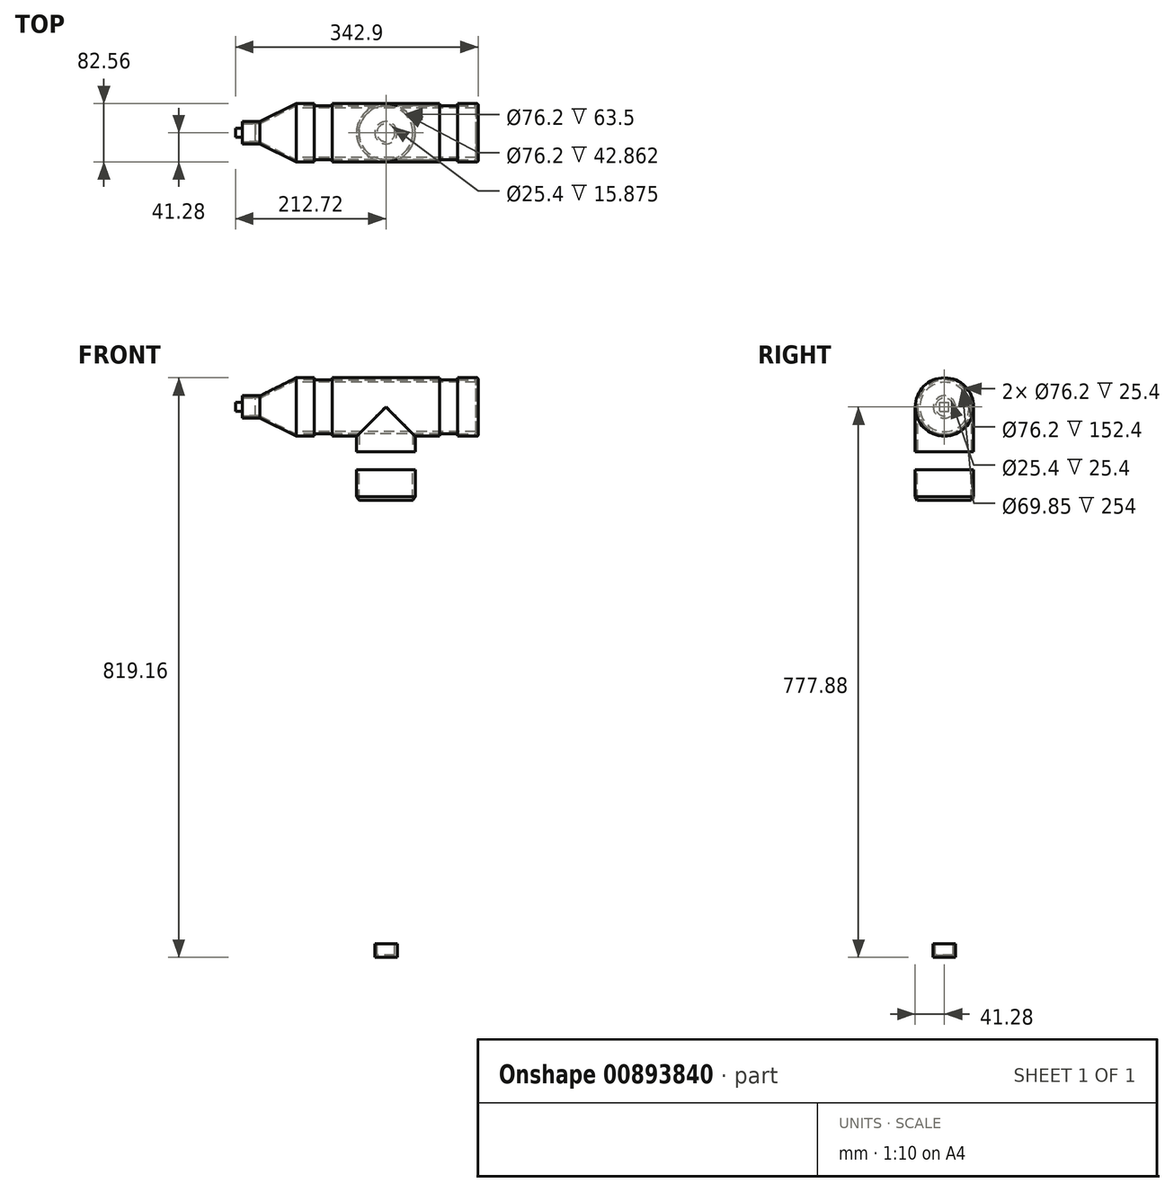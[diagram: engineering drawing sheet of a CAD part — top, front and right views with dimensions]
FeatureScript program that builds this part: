
annotation { "Feature Type Name" : "Feature", "Feature Type Description" : "" }
export const myFeature = defineFeature(function(context is Context, id is Id, definition is map)
    precondition{}
    {
        {
            var Q0;
            Q0=qCreatedBy(makeId("Top.planeOp"),FACE);
            var sketch = newSketch(context, id + "F0", { "sketchPlane" : qUnion([Q0])});
            skCircle(sketch, "E0", {"center": v(0, 0) * mm, "radius": 9.53 * mm});
            skCircle(sketch, "E1", {"center": v(0, 0) * mm, "radius": 12.7 * mm});
            skSolve(sketch);
        }
        {
            var Q0;
            Q0=makeQuery(id+"F0.imprint","IMPRINT",FACE,{"disambiguationData":[TD([[makeQuery(id+"F0.imprint","IMPRINT",EDGE,{"derivedFrom":sQuery(id+"F0.wireOp",EDGE,"E0")}),-1.0]])]});
            extrude(context, id + "F1", {"entities" : qUnion([Q0]), "depth" : 609.6 * mm, "offsetDistance" : 25.4 * mm});
        }
        {
            var Q0;
            Q0=qCreatedBy(makeId("Front.planeOp"),FACE);
            var sketch = newSketch(context, id + "F2", { "sketchPlane" : qUnion([Q0])});
            skLineSegment(sketch, "E2", {"start": v(12.7, 584.2) * mm, "end": v(12.7, 609.6) * mm});
            skLineSegment(sketch, "E3", {"start": v(12.7, 584.2) * mm, "end": v(15.87, 584.2) * mm});
            skLineSegment(sketch, "E4", {"start": v(15.87, 584.2) * mm, "end": v(15.87, 609.6) * mm});
            skLineSegment(sketch, "E5", {"start": v(38.1, 647.7) * mm, "end": v(38.1, 685.8) * mm});
            skLineSegment(sketch, "E6", {"start": v(38.1, 685.8) * mm, "end": v(41.27, 685.8) * mm});
            skLineSegment(sketch, "E7", {"start": v(41.27, 685.8) * mm, "end": v(41.27, 647.7) * mm});
            skLineSegment(sketch, "E8", {"start": v(38.1, 647.7) * mm, "end": v(12.7, 609.6) * mm});
            skLineSegment(sketch, "E9", {"start": v(41.27, 647.7) * mm, "end": v(15.87, 609.6) * mm});
            skLineSegment(sketch, "E10", {"start": v(0, 685.8) * mm, "end": v(0, 584.2) * mm, "construction": true});
            skSolve(sketch);
        }
        {
            var Q0;
            Q0=makeQuery(id+"F2.imprint","IMPRINT",FACE,{"disambiguationData":[TD([[makeQuery(id+"F2.imprint","IMPRINT",EDGE,{"derivedFrom":sQuery(id+"F2.wireOp",EDGE,"E2")}),-1.0]])]});
            var Q1;
            Q1=sQuery(id+"F2.wireOp",EDGE,"E10");
            revolve(context, id + "F3", {"surfaceOperationType" : NewSurfaceOperationType.NEW, "entities" : qUnion([Q0]), "axis" : qUnion([Q1]), "revolveType" : RevolveType.FULL});
        }
        {
            var Q0;
            Q0=qCreatedBy(makeId("Top.planeOp"),FACE);
            var sketch = newSketch(context, id + "F4", { "sketchPlane" : qUnion([Q0])});
            skCircle(sketch, "E11", {"center": v(0, 0) * mm, "radius": 38.1 * mm});
            skCircle(sketch, "E12", {"center": v(0, 0) * mm, "radius": 34.93 * mm});
            skSolve(sketch);
        }
        {
            var Q0;
            Q0 = qSketchRegion(id + "F4", true);
            extrude(context, id + "F5", {"entities" : qUnion([Q0]), "depth" : 736.6 * mm, "offsetDistance" : 25.4 * mm, "hasSecondDirection" : true, "secondDirectionOppositeDirection" : false, "secondDirectionDepth" : 647.7 * mm});
        }
        {
            var Q0;
            Q0=makeQuery(id+"F3.opRevolve","SWEPT_FACE",FACE,{"disambiguationData":[OSD([sQuery(id+"F2.wireOp",EDGE,"E6")])]});
            extrude(context, id + "F6", {"entities" : qUnion([Q0]), "depth" : 88.9 * mm, "offsetDistance" : 25.4 * mm, "hasSecondDirection" : true, "secondDirectionOppositeDirection" : false, "secondDirectionDepth" : 25.4 * mm});
        }
        {
            var Q0;
            Q0=qCreatedBy(makeId("Right.planeOp"),FACE);
            var sketch = newSketch(context, id + "F7", { "sketchPlane" : qUnion([Q0])});
            skCircle(sketch, "E13", {"center": v(0, 774.7) * mm, "radius": 41.28 * mm});
            skCircle(sketch, "E14", {"center": v(0, 774.7) * mm, "radius": 38.1 * mm});
            skLineSegment(sketch, "E15", {"start": v(-38.1, 774.7) * mm, "end": v(-38.1, 758.83) * mm});
            skLineSegment(sketch, "E16", {"start": v(38.1, 774.7) * mm, "end": v(38.1, 758.83) * mm});
            skSolve(sketch);
        }
        {
            var Q0;
            Q0=makeQuery(id+"F7.imprint","IMPRINT",FACE,{"disambiguationData":[TD([[makeQuery(id+"F7.imprint","IMPRINT",EDGE,{"derivedFrom":sQuery(id+"F7.wireOp",EDGE,"E14")}),1.0]])]});
            extrude(context, id + "F8", {"entities" : qUnion([Q0]), "operationType" : NewBodyOperationType.REMOVE, "oppositeDirection" : true, "depth" : 50.8 * mm, "offsetDistance" : 25.4 * mm, "hasSecondDirection" : true, "secondDirectionOppositeDirection" : false, "secondDirectionDepth" : 50.8 * mm});
        }
        {
            var Q0;
            {var subQ0=sQuery(id+"F7.wireOp",EDGE,"E15");Q0=makeQuery(id+"F7.imprint","IMPRINT",FACE,{"disambiguationData":[TD([[makeQuery(id+"F7.imprint","IMPRINT",EDGE,{"derivedFrom":subQ0}),-1.0]])]});}
            var Q1;
            {var subQ0=sQuery(id+"F7.wireOp",EDGE,"E15");Q1=makeQuery(id+"F7.imprint","IMPRINT",FACE,{"disambiguationData":[TD([[makeQuery(id+"F7.imprint","IMPRINT",EDGE,{"derivedFrom":subQ0}),1.0]])]});}
            extrude(context, id + "F9", {"entities" : qUnion([Q0, Q1]), "operationType" : NewBodyOperationType.ADD, "depth" : 76.2 * mm, "offsetDistance" : 25.4 * mm, "hasSecondDirection" : true, "secondDirectionOppositeDirection" : true, "secondDirectionDepth" : 76.2 * mm});
        }
        {
            var Q0;
            Q0=qCreatedBy(makeId("Top.planeOp"),FACE);
            var sketch = newSketch(context, id + "F10", { "sketchPlane" : qUnion([Q0])});
            skCircle(sketch, "E17", {"center": v(0, 0) * mm, "radius": 38.1 * mm});
            skSolve(sketch);
        }
        {
            var Q0;
            Q0=makeQuery(id+"F10.imprint","IMPRINT",FACE,{"disambiguationData":[TD([[makeQuery(id+"F10.imprint","IMPRINT",EDGE,{"derivedFrom":sQuery(id+"F10.wireOp",EDGE,"E17")}),1.0]])]});
            extrude(context, id + "F11", {"entities" : qUnion([Q0]), "operationType" : NewBodyOperationType.REMOVE, "depth" : 774.7 * mm, "offsetDistance" : 25.4 * mm});
        }
        {
            var Q0;
            Q0=qCreatedBy(makeId("Right.planeOp"),FACE);
            var sketch = newSketch(context, id + "F12", { "sketchPlane" : qUnion([Q0])});
            skCircle(sketch, "E18", {"center": v(0, 774.7) * mm, "radius": 38.1 * mm});
            skCircle(sketch, "E19", {"center": v(0, 774.7) * mm, "radius": 34.93 * mm});
            skSolve(sketch);
        }
        {
            var Q0;
            Q0=makeQuery(id+"F12.imprint","IMPRINT",FACE,{"disambiguationData":[TD([[makeQuery(id+"F12.imprint","IMPRINT",EDGE,{"derivedFrom":sQuery(id+"F12.wireOp",EDGE,"E18")}),1.0]])]});
            extrude(context, id + "F13", {"entities" : qUnion([Q0]), "depth" : 127 * mm, "offsetDistance" : 25.4 * mm, "hasSecondDirection" : true, "secondDirectionOppositeDirection" : true, "secondDirectionDepth" : 127 * mm});
        }
        {
            var Q0;
            Q0=qCreatedBy(makeId("Front.planeOp"),FACE);
            var sketch = newSketch(context, id + "F14", { "sketchPlane" : qUnion([Q0])});
            skLineSegment(sketch, "E20.bottom", {"start": v(130.17, 733.43) * mm, "end": v(101.6, 733.43) * mm});
            skLineSegment(sketch, "E20.top", {"start": v(128.59, 815.98) * mm, "end": v(101.6, 815.98) * mm});
            skLineSegment(sketch, "E20.left", {"start": v(130.17, 733.43) * mm, "end": v(130.17, 814.39) * mm});
            skLineSegment(sketch, "E20.right", {"start": v(101.6, 733.43) * mm, "end": v(101.6, 736.6) * mm});
            skPoint(sketch, "E20.middle", {"position": v(115.89, 774.7) * mm});
            skLineSegment(sketch, "E21", {"start": v(101.6, 812.8) * mm, "end": v(127, 812.8) * mm});
            skLineSegment(sketch, "E22", {"start": v(127, 812.8) * mm, "end": v(127, 736.6) * mm});
            skLineSegment(sketch, "E23", {"start": v(127, 736.6) * mm, "end": v(101.6, 736.6) * mm});
            skLineSegment(sketch, "E24.trimOffspring", {"start": v(101.6, 812.8) * mm, "end": v(101.6, 815.98) * mm});
            skLineSegment(sketch, "E25", {"start": v(130.17, 774.7) * mm, "end": v(101.6, 774.7) * mm});
            skPoint(sketch, "E26.visualSharp", {"position": v(130.17, 815.98) * mm});
            skArc(sketch, "E26.filletArc", {"start": v(130.17, 814.39) * mm, "mid": v(129.71, 815.51) * mm, "end": v(128.59, 815.98) * mm});
            skSolve(sketch);
        }
        {
            var Q0;
            Q0=makeQuery(id+"F14.imprint","IMPRINT",FACE,{"disambiguationData":[TD([[makeQuery(id+"F14.imprint","IMPRINT",EDGE,{"derivedFrom":sQuery(id+"F14.wireOp",EDGE,"E20.top")}),1.0]])]});
            var Q1;
            Q1=sQuery(id+"F14.wireOp",EDGE,"E25");
            revolve(context, id + "F15", {"surfaceOperationType" : NewSurfaceOperationType.NEW, "entities" : qUnion([Q0]), "axis" : qUnion([Q1]), "revolveType" : RevolveType.FULL});
        }
        {
            var Q0;
            Q0=qCreatedBy(makeId("Front.planeOp"),FACE);
            var sketch = newSketch(context, id + "F16", { "sketchPlane" : qUnion([Q0])});
            skLineSegment(sketch, "E27", {"start": v(-101.6, 812.8) * mm, "end": v(-127, 812.8) * mm});
            skLineSegment(sketch, "E28", {"start": v(-101.6, 812.8) * mm, "end": v(-101.6, 815.98) * mm});
            skLineSegment(sketch, "E29", {"start": v(-101.6, 815.98) * mm, "end": v(-127, 815.98) * mm});
            skLineSegment(sketch, "E30", {"start": v(-127, 812.8) * mm, "end": v(-177.8, 787.4) * mm});
            skLineSegment(sketch, "E31", {"start": v(-127, 815.98) * mm, "end": v(-177.8, 790.58) * mm});
            skLineSegment(sketch, "E32", {"start": v(-177.8, 790.58) * mm, "end": v(-203.2, 790.58) * mm});
            skLineSegment(sketch, "E33", {"start": v(-203.2, 790.58) * mm, "end": v(-203.2, 787.4) * mm});
            skLineSegment(sketch, "E34", {"start": v(-203.2, 787.4) * mm, "end": v(-177.8, 787.4) * mm});
            skLineSegment(sketch, "E35", {"start": v(-203.2, 774.7) * mm, "end": v(-101.6, 774.7) * mm, "construction": true});
            skSolve(sketch);
        }
        {
            var Q0;
            Q0=makeQuery(id+"F16.imprint","IMPRINT",FACE,{"disambiguationData":[TD([[makeQuery(id+"F16.imprint","IMPRINT",EDGE,{"derivedFrom":sQuery(id+"F16.wireOp",EDGE,"E27")}),-1.0]])]});
            var Q1;
            Q1=sQuery(id+"F16.wireOp",EDGE,"E35");
            revolve(context, id + "F17", {"surfaceOperationType" : NewSurfaceOperationType.NEW, "entities" : qUnion([Q0]), "axis" : qUnion([Q1]), "revolveType" : RevolveType.FULL});
        }
        {
            var Q0;
            Q0=qCreatedBy(makeId("Right.planeOp"),FACE);
            var sketch = newSketch(context, id + "F18", { "sketchPlane" : qUnion([Q0])});
            skCircle(sketch, "E36", {"center": v(0, 774.7) * mm, "radius": 12.7 * mm});
            skLineSegment(sketch, "E37.bottom", {"start": v(-6.35, 768.35) * mm, "end": v(6.35, 768.35) * mm});
            skLineSegment(sketch, "E37.top", {"start": v(-6.35, 781.05) * mm, "end": v(6.35, 781.05) * mm});
            skLineSegment(sketch, "E37.left", {"start": v(-6.35, 768.35) * mm, "end": v(-6.35, 781.05) * mm});
            skLineSegment(sketch, "E37.right", {"start": v(6.35, 768.35) * mm, "end": v(6.35, 781.05) * mm});
            skSolve(sketch);
        }
        {
            var Q0;
            Q0=makeQuery(id+"F18.imprint","IMPRINT",FACE,{"disambiguationData":[TD([[makeQuery(id+"F18.imprint","IMPRINT",EDGE,{"derivedFrom":sQuery(id+"F18.wireOp",EDGE,"E36")}),1.0]])]});
            var Q1;
            Q1=makeQuery(id+"F18.imprint","IMPRINT",FACE,{"disambiguationData":[TD([[makeQuery(id+"F18.imprint","IMPRINT",EDGE,{"derivedFrom":sQuery(id+"F18.wireOp",EDGE,"E37.bottom")}),1.0]])]});
            extrude(context, id + "F19", {"entities" : qUnion([Q0, Q1]), "oppositeDirection" : true, "depth" : 203.2 * mm, "offsetDistance" : 25.4 * mm, "hasSecondDirection" : true, "secondDirectionOppositeDirection" : true, "secondDirectionDepth" : 184.15 * mm});
        }
        {
            var Q0;
            Q0=makeQuery(id+"F18.imprint","IMPRINT",FACE,{"disambiguationData":[TD([[makeQuery(id+"F18.imprint","IMPRINT",EDGE,{"derivedFrom":sQuery(id+"F18.wireOp",EDGE,"E37.bottom")}),1.0]])]});
            extrude(context, id + "F20", {"entities" : qUnion([Q0]), "operationType" : NewBodyOperationType.ADD, "oppositeDirection" : true, "depth" : 212.72 * mm, "offsetDistance" : 25.4 * mm, "hasSecondDirection" : true, "secondDirectionOppositeDirection" : true, "secondDirectionDepth" : 184.15 * mm, "hasSecondDirectionDraft" : true, "secondDirectionDraftAngle" : 3 * degree});
        }
        {
            var Q0;
            Q0=qCreatedBy(makeId("Front.planeOp"),FACE);
            var sketch = newSketch(context, id + "F21", { "sketchPlane" : qUnion([Q0])});
            skLineSegment(sketch, "E38", {"start": v(12.7, 15.88) * mm, "end": v(12.7, 0) * mm});
            skLineSegment(sketch, "E39", {"start": v(12.7, 0) * mm, "end": v(0, 0) * mm});
            skLineSegment(sketch, "E40", {"start": v(0, 0) * mm, "end": v(0, -3.18) * mm});
            skLineSegment(sketch, "E41", {"start": v(0, -3.18) * mm, "end": v(15.88, -3.18) * mm});
            skLineSegment(sketch, "E42", {"start": v(15.88, -3.17) * mm, "end": v(15.88, 15.88) * mm});
            skLineSegment(sketch, "E43", {"start": v(15.88, 15.88) * mm, "end": v(12.7, 15.88) * mm});
            skLineSegment(sketch, "E44", {"start": v(0, 15.88) * mm, "end": v(0, 0) * mm, "construction": true});
            skSolve(sketch);
        }
        {
            var Q0;
            Q0=makeQuery(id+"F21.imprint","IMPRINT",FACE,{"disambiguationData":[TD([[makeQuery(id+"F21.imprint","IMPRINT",EDGE,{"derivedFrom":sQuery(id+"F21.wireOp",EDGE,"E38")}),1.0]])]});
            var Q1;
            Q1=sQuery(id+"F21.wireOp",EDGE,"E40");
            revolve(context, id + "F22", {"operationType" : NewBodyOperationType.ADD, "surfaceOperationType" : NewSurfaceOperationType.NEW, "entities" : qUnion([Q0]), "axis" : qUnion([Q1]), "revolveType" : RevolveType.FULL});
        }
    });
